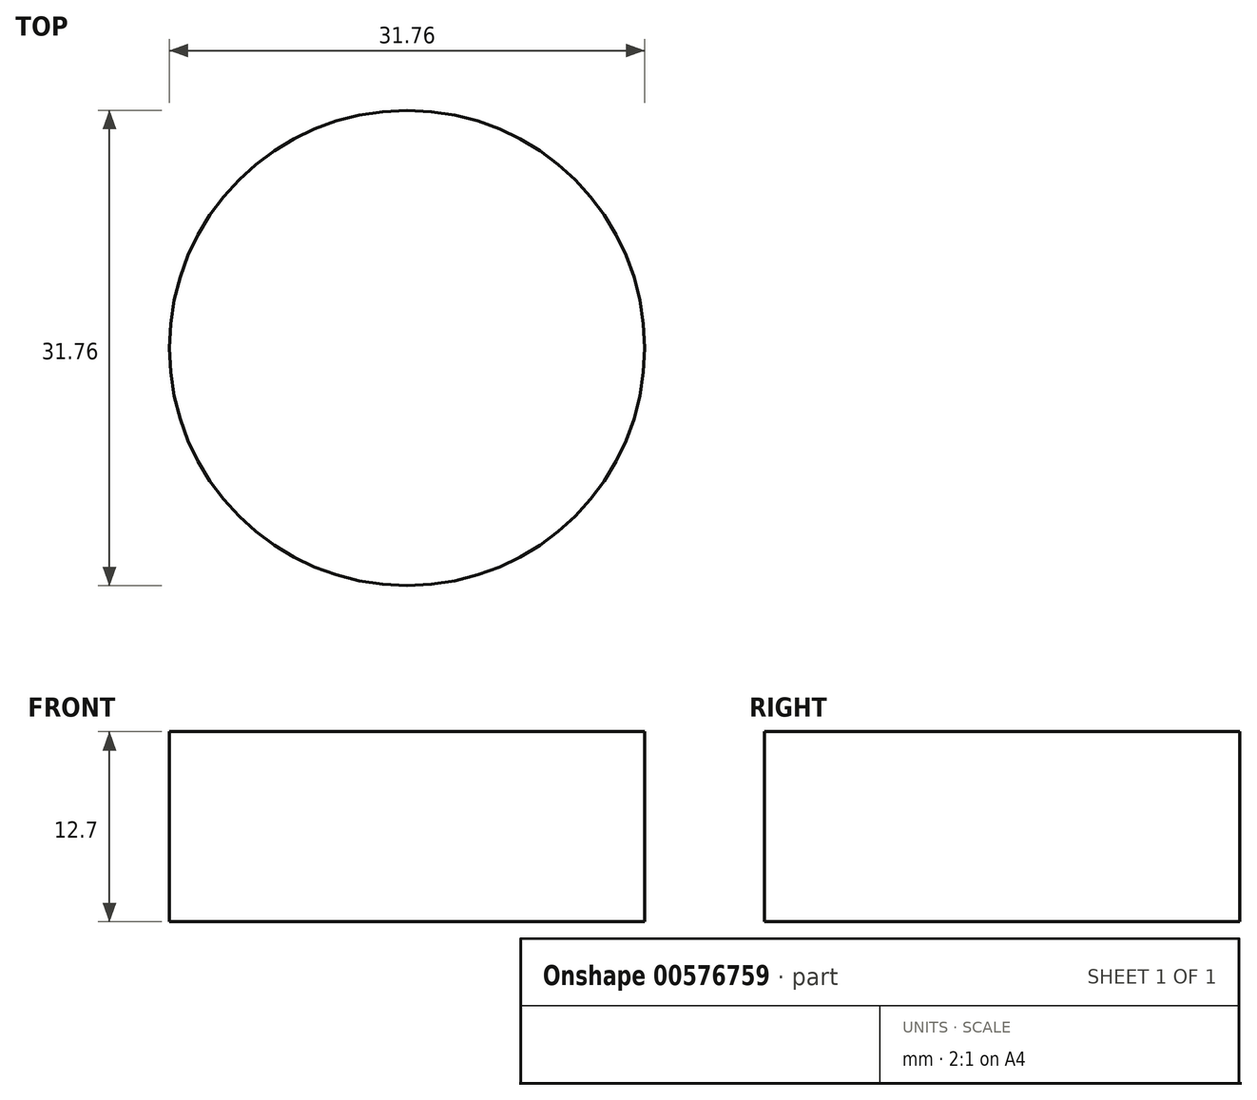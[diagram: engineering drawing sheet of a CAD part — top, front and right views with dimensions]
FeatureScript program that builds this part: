
annotation { "Feature Type Name" : "Feature", "Feature Type Description" : "" }
export const myFeature = defineFeature(function(context is Context, id is Id, definition is map)
    precondition{}
    {
        {
            var Q0;
            Q0=qCreatedBy(makeId("Top.planeOp"),FACE);
            var sketch = newSketch(context, id + "F0", { "sketchPlane" : qUnion([Q0])});
            skCircle(sketch, "E0", {"center": v(0, 0) * mm, "radius": 15.88 * mm});
            skSolve(sketch);
        }
        {
            var Q0;
            Q0=makeQuery(id+"F0.imprint","IMPRINT",FACE,{"disambiguationData":[TD([[makeQuery(id+"F0.imprint","IMPRINT",EDGE,{"derivedFrom":sQuery(id+"F0.wireOp",EDGE,"E0")}),1.0]])]});
            extrude(context, id + "F1", {"entities" : qUnion([Q0]), "depth" : 12.7 * mm, "offsetDistance" : 25.4 * mm});
        }
    });
